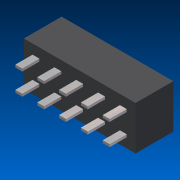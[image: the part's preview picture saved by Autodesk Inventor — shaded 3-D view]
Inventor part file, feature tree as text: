
AUTODESK INVENTOR PART (.ipt)
format: ipt  version: 2015 SP1 (Build 190203100, 203)  size: 185,856 bytes
history: native  units: mm
features: extrude x3, sketch x3, other x1
ambient origin geometry x8: Origin, YZ Plane, XZ Plane, XY Plane, X Axis, Y Axis, Z Axis, Center Point
bodies: Body1 (feature_tree)
feature tree (7):
  other  "Твердое тело1"
  extrude  "Выдавливание1"  Depth=13.0mm
  extrude  "Выдавливание2"  Depth=5.08mm
  extrude  "Выдавливание3"  Depth=4.4mm TaperAngle=0.0deg
  sketch  "Эскиз1"
  sketch  "Эскиз2"
  sketch  "Эскиз3"
